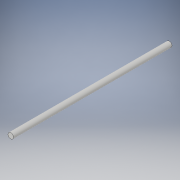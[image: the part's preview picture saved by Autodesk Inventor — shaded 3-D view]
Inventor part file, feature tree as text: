
AUTODESK INVENTOR PART (.ipt)
format: ipt  version: 2018 (Build 220112000, 112)  size: 90,112 bytes
history: native  units: in
note: dims shown in document units (in); Inventor stores cm internally (conversion verified against a paired STEP export)
features: extrude x1, sketch x1
ambient origin geometry x8: Origin, YZ Plane, XZ Plane, XY Plane, X Axis, Y Axis, Z Axis, Center Point
bodies: Solid1 (feature_tree)
feature tree (2):
  extrude  "Extrusion1"  Depth=144.0in TaperAngle=0.0deg
  sketch  "Sketch1"  dims[d0=5.0in d1=144.0in d2=0.0in]
